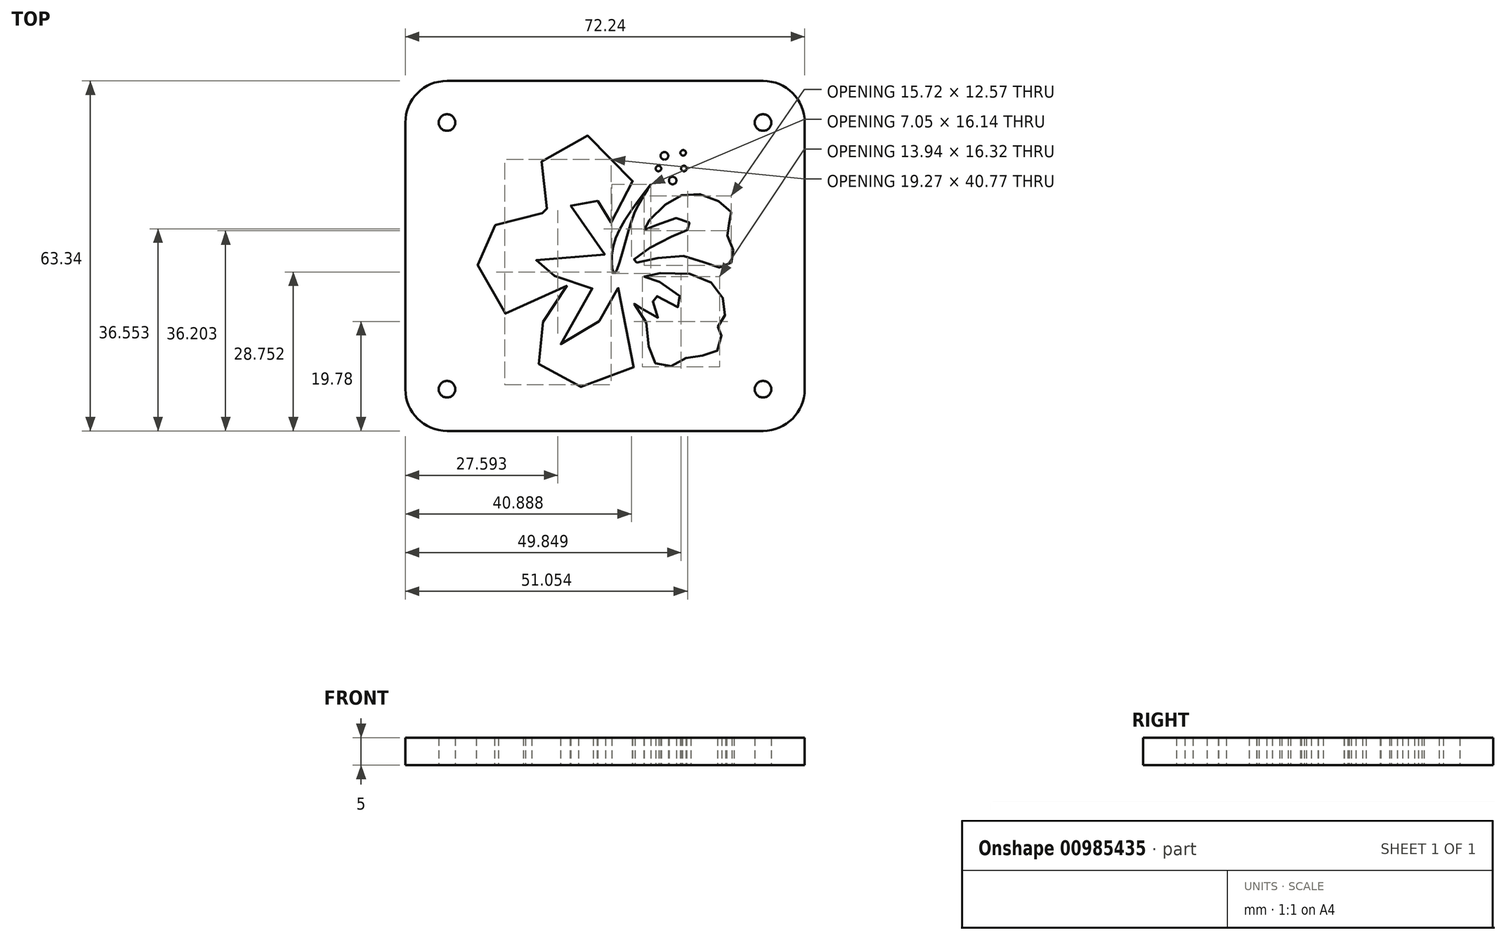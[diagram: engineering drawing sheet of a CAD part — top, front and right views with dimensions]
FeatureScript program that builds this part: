
annotation { "Feature Type Name" : "Feature", "Feature Type Description" : "" }
export const myFeature = defineFeature(function(context is Context, id is Id, definition is map)
    precondition{}
    {
        {
            var Q0;
            Q0=qCreatedBy(makeId("Top.planeOp"),FACE);
            var sketch = newSketch(context, id + "F0", { "sketchPlane" : qUnion([Q0])});
            skLineSegment(sketch, "E0.bottom", {"start": v(-28.57, -31.67) * mm, "end": v(28.58, -31.67) * mm});
            skLineSegment(sketch, "E0.top", {"start": v(-28.58, 31.67) * mm, "end": v(28.57, 31.67) * mm});
            skLineSegment(sketch, "E0.left", {"start": v(-36.12, -24.13) * mm, "end": v(-36.12, 24.13) * mm});
            skLineSegment(sketch, "E0.right", {"start": v(36.12, -24.13) * mm, "end": v(36.11, 24.13) * mm});
            skPoint(sketch, "E0.middle", {"position": v(0, 0) * mm});
            skPoint(sketch, "E1.visualSharp", {"position": v(-36.12, 31.67) * mm});
            skArc(sketch, "E1.filletArc", {"start": v(-28.58, 31.67) * mm, "mid": v(-33.9, 29.46) * mm, "end": v(-36.12, 24.13) * mm});
            skPoint(sketch, "E2.visualSharp", {"position": v(36.11, 31.67) * mm});
            skArc(sketch, "E2.filletArc", {"start": v(36.11, 24.13) * mm, "mid": v(33.9, 29.46) * mm, "end": v(28.57, 31.67) * mm});
            skPoint(sketch, "E3.visualSharp", {"position": v(-36.11, -31.67) * mm});
            skArc(sketch, "E3.filletArc", {"start": v(-36.11, -24.13) * mm, "mid": v(-33.9, -29.46) * mm, "end": v(-28.57, -31.67) * mm});
            skPoint(sketch, "E4.visualSharp", {"position": v(36.12, -31.67) * mm});
            skArc(sketch, "E4.filletArc", {"start": v(28.58, -31.67) * mm, "mid": v(33.9, -29.46) * mm, "end": v(36.12, -24.13) * mm});
            skCircle(sketch, "E5", {"center": v(-28.58, 24.13) * mm, "radius": 1.5 * mm});
            skCircle(sketch, "E6.MirrorC", {"center": v(28.58, 24.13) * mm, "radius": 1.5 * mm});
            skCircle(sketch, "E7.MirrorC", {"center": v(28.58, -24.13) * mm, "radius": 1.5 * mm});
            skCircle(sketch, "E8.MirrorC", {"center": v(-28.58, -24.13) * mm, "radius": 1.5 * mm});
            skCircle(sketch, "E9", {"center": v(14.13, 18.65) * mm, "radius": 0.5 * mm});
            skCircle(sketch, "E10", {"center": v(10.74, 18.11) * mm, "radius": 0.7 * mm});
            skFitSpline(sketch, "E11", {"points": [v(1.1, 6.04) * mm, v(2.84, 10.54) * mm, v(4.96, 13.25) * mm, v(1.8, 18.33) * mm, v(-4.82, 21.83) * mm, v(-9.31, 18.06) * mm, v(-13.26, 16.36) * mm, v(-13.91, 12.61) * mm, v(-6.18, 4.74) * mm, v(-12.84, 8.05) * mm, v(-17.3, 5.47) * mm, v(-19.91, 5.52) * mm, v(-19.3, 2.56) * mm, v(-23.02, -1.63) * mm, v(-21.5, -7.05) * mm, v(-16.81, -10.69) * mm, v(-8.82, -6.35) * mm, v(-4.82, -5.17) * mm, v(-12.47, -13.24) * mm, v(-14.53, -17.9) * mm, v(-11.26, -20.19) * mm, v(-9.4, -23.74) * mm, v(0, -22.83) * mm, v(4.4, -21.71) * mm, v(4.94, -13.07) * mm, v(1.63, -5.52) * mm, v(0, -12.42) * mm, v(-2.53, -11.1) * mm, v(-7.6, -16.6) * mm, v(-6.52, -10.19) * mm, v(-2.24, -5.72) * mm, v(-3.46, -3.31) * mm, v(-8.7, -3.3) * mm, v(-12.4, -6.53) * mm, v(-11.72, 0) * mm, v(0, 0) * mm, v(-1.63, 1.57) * mm, v(-5.81, 7.64) * mm, v(-5.81, 11.34) * mm, v(-1.74, 8.73) * mm, v(-1.38, 13.24) * mm, v(1.1, 6.04) * mm]});
            skFitSpline(sketch, "E12", {"points": [v(7.08, 4.68) * mm, v(10.74, 9.16) * mm, v(17.52, 11.06) * mm, v(22.95, 7.53) * mm, v(22, 4.55) * mm, v(23.35, 0) * mm, v(21.05, -2.1) * mm, v(13.72, 0) * mm, v(4.96, -1.15) * mm, v(11, 3.05) * mm, v(15.49, 5.36) * mm, v(13.04, 6.85) * mm, v(7.08, 4.68) * mm]});
            skFitSpline(sketch, "E13", {"points": [v(7.08, -3.73) * mm, v(14.8, -3.19) * mm, v(20.78, -6.58) * mm, v(21.59, -11.1) * mm, v(20.37, -13.09) * mm, v(21.05, -14.45) * mm, v(19.7, -17.7) * mm, v(15.62, -18.1) * mm, v(11.82, -20) * mm, v(8.43, -18.65) * mm, v(7.08, -11.1) * mm, v(4.96, -8.34) * mm, v(9.65, -11.1) * mm, v(8.3, -6.98) * mm, v(13.45, -9.3) * mm, v(12.64, -6.17) * mm, v(7.08, -3.73) * mm]});
            skFitSpline(sketch, "E14", {"points": [v(1.65, -3.19) * mm, v(3.82, 3.05) * mm, v(6.26, 9.7) * mm, v(8.3, 12.96) * mm, v(3.68, 6.58) * mm, v(1.24, 0) * mm, v(1.65, -3.19) * mm]});
            skCircle(sketch, "E15", {"center": v(14.26, 15.8) * mm, "radius": 0.5 * mm});
            skCircle(sketch, "E16", {"center": v(12.23, 13.63) * mm, "radius": 0.68 * mm});
            skCircle(sketch, "E17", {"center": v(9.65, 15.8) * mm, "radius": 0.5 * mm});
            skSolve(sketch);
        }
        {
            var Q0;
            Q0=makeQuery(id+"F0.imprint","IMPRINT",FACE,{"disambiguationData":[TD([[makeQuery(id+"F0.imprint","IMPRINT",EDGE,{"derivedFrom":sQuery(id+"F0.wireOp",EDGE,"E0.bottom")}),1.0]])]});
            extrude(context, id + "F1", {"entities" : qUnion([Q0]), "depth" : 5 * mm, "offsetDistance" : 25 * mm});
        }
    });
